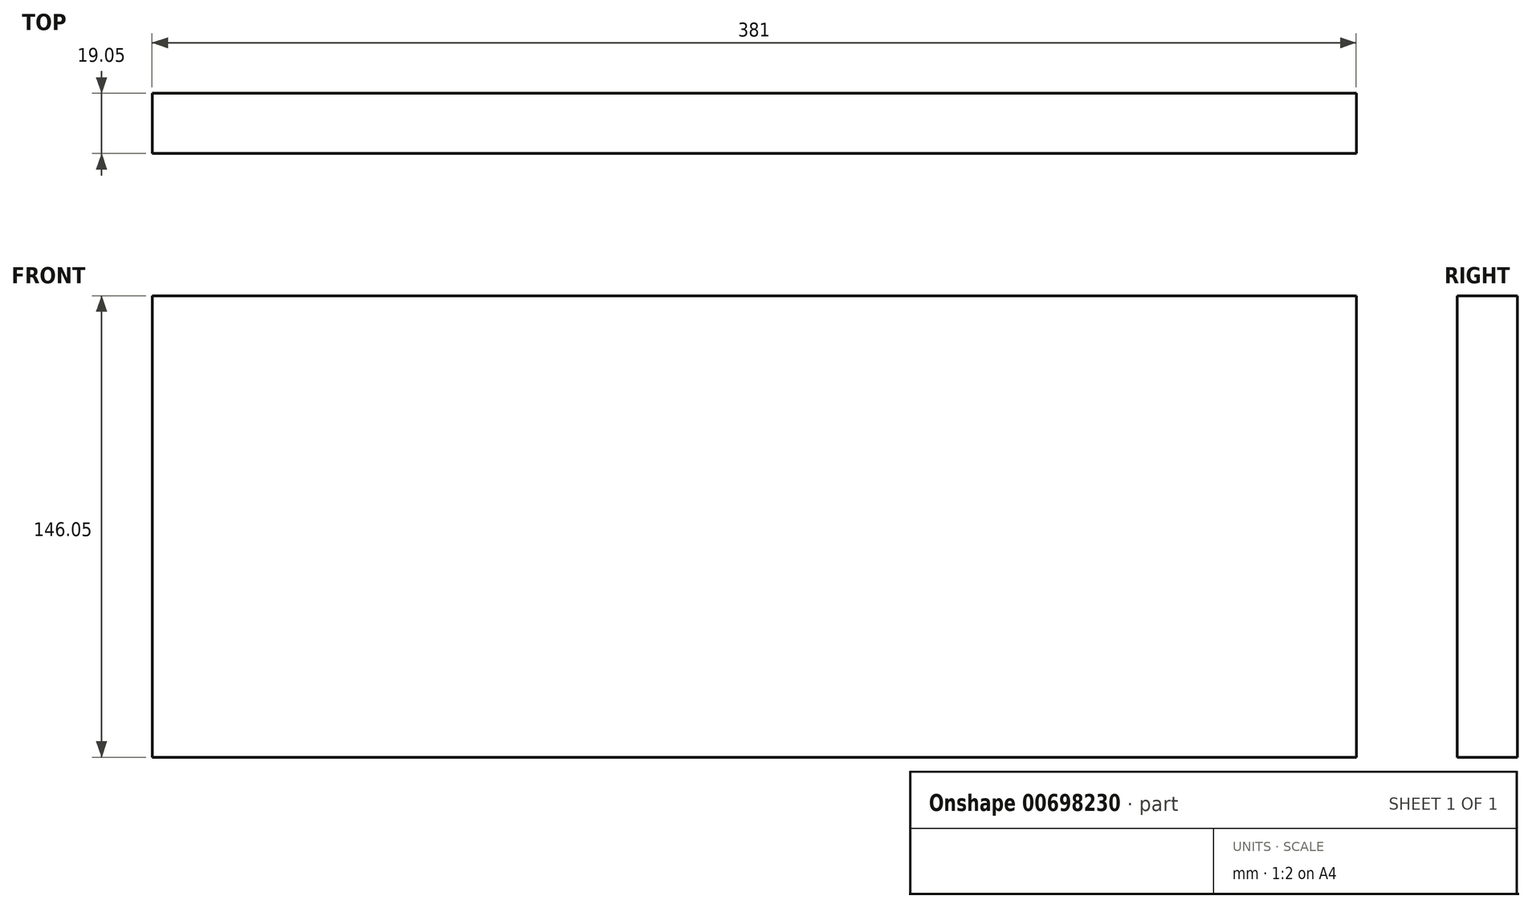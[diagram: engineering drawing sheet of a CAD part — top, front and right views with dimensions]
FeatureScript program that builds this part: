
annotation { "Feature Type Name" : "Feature", "Feature Type Description" : "" }
export const myFeature = defineFeature(function(context is Context, id is Id, definition is map)
    precondition{}
    {
        {
            var Q0;
            Q0=qCreatedBy(makeId("Right.planeOp"),FACE);
            var sketch = newSketch(context, id + "F0", { "sketchPlane" : qUnion([Q0])});
            skLineSegment(sketch, "E0.bottom", {"start": v(-190.55, 62.54) * mm, "end": v(199.77, 62.54) * mm});
            skLineSegment(sketch, "E0.top", {"start": v(-190.55, -93.38) * mm, "end": v(199.77, -93.38) * mm});
            skLineSegment(sketch, "E0.left", {"start": v(-190.55, 62.54) * mm, "end": v(-190.55, -93.38) * mm});
            skLineSegment(sketch, "E0.right", {"start": v(199.77, 62.54) * mm, "end": v(199.77, -93.38) * mm});
            skSolve(sketch);
        }
        {
            var Q0;
            Q0 = qSketchRegion(id + "F0", true);
            extrude(context, id + "F1", {"entities" : qUnion([Q0]), "depth" : 25.4 * mm, "offsetDistance" : 25.4 * mm});
        }
        {
            var Q0;
            Q0=makeQuery(id+"F1.opExtrude","SWEPT_BODY",BODY,{"disambiguationData":[OSD([sQuery(id+"F0.wireOp",EDGE,"E0.bottom"),sQuery(id+"F0.wireOp",EDGE,"E0.top"),sQuery(id+"F0.wireOp",EDGE,"E0.left"),sQuery(id+"F0.wireOp",EDGE,"E0.right")])]});
            deleteBodies(context, id + "F2", {"entities" : qUnion([Q0])});
        }
        {
            var Q0;
            Q0=qCreatedBy(makeId("Front.planeOp"),FACE);
            var sketch = newSketch(context, id + "F3", { "sketchPlane" : qUnion([Q0])});
            skLineSegment(sketch, "E1.bottom", {"start": v(-182.43, 101.46) * mm, "end": v(198.57, 101.46) * mm});
            skLineSegment(sketch, "E1.top", {"start": v(-182.43, -50.94) * mm, "end": v(198.57, -50.94) * mm});
            skLineSegment(sketch, "E1.left", {"start": v(-182.43, 101.46) * mm, "end": v(-182.43, -50.94) * mm});
            skLineSegment(sketch, "E1.right", {"start": v(198.57, 101.46) * mm, "end": v(198.57, -50.94) * mm});
            skSolve(sketch);
        }
        {
            var Q0;
            Q0=makeQuery(id+"F3.imprint","IMPRINT",FACE,{"disambiguationData":[TD([[makeQuery(id+"F3.imprint","IMPRINT",EDGE,{"derivedFrom":sQuery(id+"F3.wireOp",EDGE,"E1.bottom")}),-1.0]])]});
            extrude(context, id + "F4", {"entities" : qUnion([Q0]), "depth" : 25.4 * mm, "offsetDistance" : 25.4 * mm});
        }
        {
            var Q0;
            Q0=makeQuery(id+"F4.opExtrude","SWEPT_BODY",BODY,{"disambiguationData":[OSD([sQuery(id+"F3.wireOp",EDGE,"E1.bottom"),sQuery(id+"F3.wireOp",EDGE,"E1.top"),sQuery(id+"F3.wireOp",EDGE,"E1.left"),sQuery(id+"F3.wireOp",EDGE,"E1.right")])]});
            deleteBodies(context, id + "F5", {"entities" : qUnion([Q0])});
        }
        {
            var Q0;
            Q0=qCreatedBy(makeId("Front.planeOp"),FACE);
            var sketch = newSketch(context, id + "F6", { "sketchPlane" : qUnion([Q0])});
            skLineSegment(sketch, "E2.bottom", {"start": v(-225.92, 68.87) * mm, "end": v(155.08, 68.87) * mm});
            skLineSegment(sketch, "E2.top", {"start": v(-225.92, -77.18) * mm, "end": v(155.08, -77.18) * mm});
            skLineSegment(sketch, "E2.left", {"start": v(-225.92, 68.87) * mm, "end": v(-225.92, -77.18) * mm});
            skLineSegment(sketch, "E2.right", {"start": v(155.08, 68.87) * mm, "end": v(155.08, -77.18) * mm});
            skSolve(sketch);
        }
        {
            var Q0;
            Q0=makeQuery(id+"F6.imprint","IMPRINT",FACE,{"disambiguationData":[TD([[makeQuery(id+"F6.imprint","IMPRINT",EDGE,{"derivedFrom":sQuery(id+"F6.wireOp",EDGE,"E2.bottom")}),-1.0]])]});
            extrude(context, id + "F7", {"entities" : qUnion([Q0]), "depth" : 19.05 * mm, "offsetDistance" : 25.4 * mm});
        }
    });
